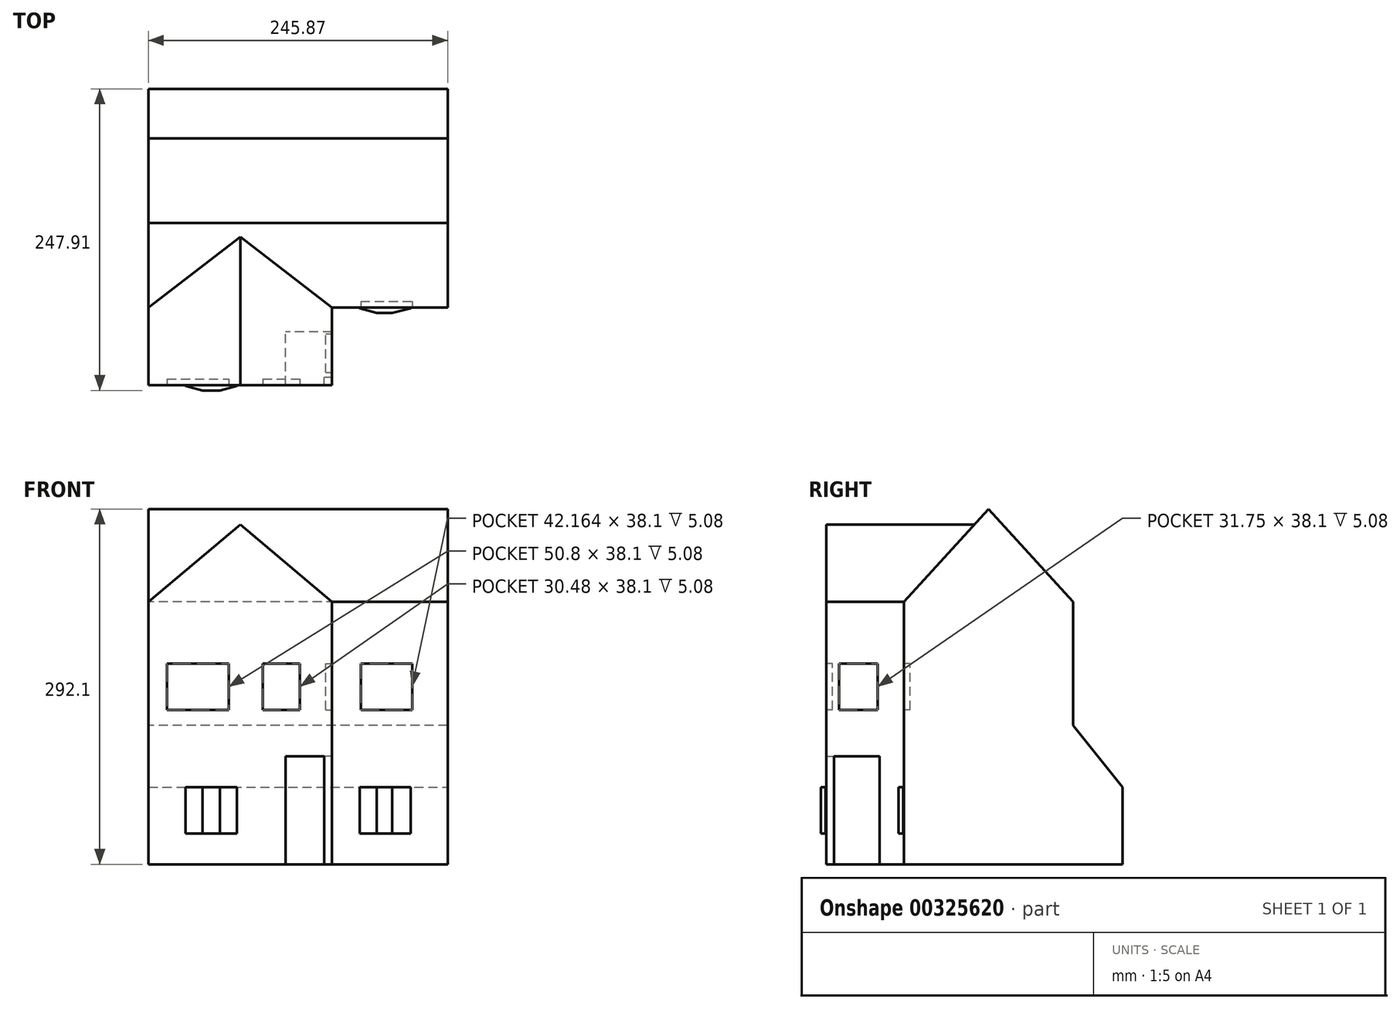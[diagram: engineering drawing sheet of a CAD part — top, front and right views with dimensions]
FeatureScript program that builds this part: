
annotation { "Feature Type Name" : "Feature", "Feature Type Description" : "" }
export const myFeature = defineFeature(function(context is Context, id is Id, definition is map)
    precondition{}
    {
        {
            var Q0;
            Q0=qCreatedBy(makeId("Top.planeOp"),FACE);
            var sketch = newSketch(context, id + "F0", { "sketchPlane" : qUnion([Q0])});
            skLineSegment(sketch, "E0", {"start": v(245.87, 63.75) * mm, "end": v(150.88, 63.75) * mm});
            skLineSegment(sketch, "E1", {"start": v(150.88, 63.75) * mm, "end": v(150.88, 0) * mm});
            skLineSegment(sketch, "E2", {"start": v(150.88, 0) * mm, "end": v(0, 0) * mm});
            skLineSegment(sketch, "E3", {"start": v(0, 0) * mm, "end": v(0, 243.59) * mm});
            skLineSegment(sketch, "E4", {"start": v(0, 243.59) * mm, "end": v(245.87, 243.59) * mm});
            skLineSegment(sketch, "E5", {"start": v(245.87, 243.59) * mm, "end": v(245.87, 63.75) * mm});
            skLineSegment(sketch, "E6.0", {"start": v(6.35, 237.24) * mm, "end": v(239.52, 237.24) * mm});
            skLineSegment(sketch, "E6.1", {"start": v(239.52, 70.1) * mm, "end": v(144.53, 70.1) * mm});
            skLineSegment(sketch, "E6.2", {"start": v(144.53, 70.1) * mm, "end": v(144.53, 6.35) * mm});
            skLineSegment(sketch, "E6.3", {"start": v(239.52, 237.24) * mm, "end": v(239.52, 70.1) * mm});
            skLineSegment(sketch, "E6.4", {"start": v(144.53, 6.35) * mm, "end": v(6.35, 6.35) * mm});
            skLineSegment(sketch, "E6.5", {"start": v(6.35, 6.35) * mm, "end": v(6.35, 237.24) * mm});
            skLineSegment(sketch, "E7", {"start": v(239.52, 195.58) * mm, "end": v(6.35, 195.58) * mm});
            skLineSegment(sketch, "E8.0", {"start": v(239.52, 201.93) * mm, "end": v(6.35, 201.93) * mm});
            skLineSegment(sketch, "E9", {"start": v(144.53, 70.1) * mm, "end": v(144.53, 237.24) * mm});
            skLineSegment(sketch, "E10.0", {"start": v(148.34, 70.1) * mm, "end": v(148.34, 237.24) * mm});
            skLineSegment(sketch, "E11", {"start": v(96.01, 6.35) * mm, "end": v(96.01, 195.58) * mm});
            skLineSegment(sketch, "E12.0", {"start": v(92.2, 6.35) * mm, "end": v(92.2, 195.58) * mm});
            skLineSegment(sketch, "E13", {"start": v(92.2, 153.16) * mm, "end": v(6.35, 153.16) * mm});
            skLineSegment(sketch, "E14.0", {"start": v(92.2, 149.35) * mm, "end": v(6.35, 149.35) * mm});
            skLineSegment(sketch, "E15", {"start": v(88.4, 201.93) * mm, "end": v(88.4, 237.24) * mm});
            skLineSegment(sketch, "E16.0", {"start": v(92.2, 201.93) * mm, "end": v(92.2, 237.24) * mm});
            skSolve(sketch);
        }
        {
            var Q0;
            Q0=makeQuery(id+"F0.imprint","IMPRINT",FACE,{"disambiguationData":[TD([[makeQuery(id+"F0.imprint","IMPRINT",EDGE,{"derivedFrom":sQuery(id+"F0.wireOp",EDGE,"E0")}),-1.0]])]});
            var Q1;
            {var subQ0=sQuery(id+"F0.wireOp",EDGE,"E10.0");var subQ1=sQuery(id+"F0.wireOp",EDGE,"E7");var subQ2=makeQuery(id+"F0.imprint","INTERSECT",VERTEX,{"derivedFrom":[subQ1,subQ0]});Q1=makeQuery(id+"F0.imprint","IMPRINT",FACE,{"disambiguationData":[TD([[makeQuery(id+"F0.imprint","IMPRINT",EDGE,{"disambiguationData":[TD([[subQ2,-1.0]])],"derivedFrom":subQ1}),-1.0]])]});}
            var Q2;
            {var subQ0=sQuery(id+"F0.wireOp",EDGE,"E6.3");var subQ1=sQuery(id+"F0.wireOp",EDGE,"E6.1");var subQ2=makeQuery(id+"F0.imprint","INTERSECT",VERTEX,{"derivedFrom":[subQ1,subQ0]});Q2=makeQuery(id+"F0.imprint","IMPRINT",FACE,{"disambiguationData":[TD([[makeQuery(id+"F0.imprint","IMPRINT",EDGE,{"disambiguationData":[TD([[subQ2,-1.0]])],"derivedFrom":subQ1}),-1.0]])]});}
            var Q3;
            {var subQ0=sQuery(id+"F0.wireOp",EDGE,"E6.3");var subQ1=sQuery(id+"F0.wireOp",EDGE,"E6.0");var subQ2=makeQuery(id+"F0.imprint","INTERSECT",VERTEX,{"derivedFrom":[subQ1,subQ0]});Q3=makeQuery(id+"F0.imprint","IMPRINT",FACE,{"disambiguationData":[TD([[makeQuery(id+"F0.imprint","IMPRINT",EDGE,{"disambiguationData":[TD([[subQ2,1.0]])],"derivedFrom":subQ1}),-1.0]])]});}
            var Q4;
            {var subQ3=sQuery(id+"F0.wireOp",EDGE,"E16.0");Q4=makeQuery(id+"F0.imprint","IMPRINT",FACE,{"disambiguationData":[TD([[makeQuery(id+"F0.imprint","IMPRINT",EDGE,{"derivedFrom":subQ3}),-1.0]])]});}
            var Q5;
            {var subQ3=sQuery(id+"F0.wireOp",EDGE,"E15");Q5=makeQuery(id+"F0.imprint","IMPRINT",FACE,{"disambiguationData":[TD([[makeQuery(id+"F0.imprint","IMPRINT",EDGE,{"derivedFrom":subQ3}),1.0]])]});}
            var Q6;
            {var subQ3=sQuery(id+"F0.wireOp",EDGE,"E13");Q6=makeQuery(id+"F0.imprint","IMPRINT",FACE,{"disambiguationData":[TD([[makeQuery(id+"F0.imprint","IMPRINT",EDGE,{"derivedFrom":subQ3}),-1.0]])]});}
            var Q7;
            {var subQ1=sQuery(id+"F0.wireOp",EDGE,"E6.2");Q7=makeQuery(id+"F0.imprint","IMPRINT",FACE,{"disambiguationData":[TD([[makeQuery(id+"F0.imprint","IMPRINT",EDGE,{"derivedFrom":subQ1}),-1.0]])]});}
            var Q8;
            {var subQ3=sQuery(id+"F0.wireOp",EDGE,"E10.0");var subQ5=sQuery(id+"F0.wireOp",EDGE,"E7");var subQ6=makeQuery(id+"F0.imprint","INTERSECT",VERTEX,{"derivedFrom":[subQ5,subQ3]});Q8=makeQuery(id+"F0.imprint","IMPRINT",FACE,{"disambiguationData":[TD([[makeQuery(id+"F0.imprint","IMPRINT",EDGE,{"disambiguationData":[TD([[subQ6,-1.0]])],"derivedFrom":subQ5}),1.0]])]});}
            var Q9;
            {var subQ5=sQuery(id+"F0.wireOp",EDGE,"E14.0");Q9=makeQuery(id+"F0.imprint","IMPRINT",FACE,{"disambiguationData":[TD([[makeQuery(id+"F0.imprint","IMPRINT",EDGE,{"derivedFrom":subQ5}),1.0]])]});}
            var Q10;
            {var subQ4=sQuery(id+"F0.wireOp",EDGE,"E11");Q10=makeQuery(id+"F0.imprint","IMPRINT",FACE,{"disambiguationData":[TD([[makeQuery(id+"F0.imprint","IMPRINT",EDGE,{"derivedFrom":subQ4}),1.0]])]});}
            var Q11;
            {var subQ0=sQuery(id+"F0.wireOp",EDGE,"E13");Q11=makeQuery(id+"F0.imprint","IMPRINT",FACE,{"disambiguationData":[TD([[makeQuery(id+"F0.imprint","IMPRINT",EDGE,{"derivedFrom":subQ0}),1.0]])]});}
            var Q12;
            {var subQ0=sQuery(id+"F0.wireOp",EDGE,"E7");var subQ1=sQuery(id+"F0.wireOp",EDGE,"E6.3");var subQ2=makeQuery(id+"F0.imprint","INTERSECT",VERTEX,{"derivedFrom":[subQ1,subQ0]});Q12=makeQuery(id+"F0.imprint","IMPRINT",FACE,{"disambiguationData":[TD([[makeQuery(id+"F0.imprint","IMPRINT",EDGE,{"disambiguationData":[TD([[subQ2,1.0]])],"derivedFrom":subQ1}),-1.0]])]});}
            var Q13;
            {var subQ0=sQuery(id+"F0.wireOp",EDGE,"E7");var subQ1=sQuery(id+"F0.wireOp",EDGE,"E6.5");var subQ2=makeQuery(id+"F0.imprint","INTERSECT",VERTEX,{"derivedFrom":[subQ1,subQ0]});Q13=makeQuery(id+"F0.imprint","IMPRINT",FACE,{"disambiguationData":[TD([[makeQuery(id+"F0.imprint","IMPRINT",EDGE,{"disambiguationData":[TD([[subQ2,-1.0]])],"derivedFrom":subQ1}),-1.0]])]});}
            var Q14;
            {var subQ0=sQuery(id+"F0.wireOp",EDGE,"E9");var subQ1=sQuery(id+"F0.wireOp",EDGE,"E6.0");var subQ2=makeQuery(id+"F0.imprint","INTERSECT",VERTEX,{"derivedFrom":[subQ1,subQ0]});Q14=makeQuery(id+"F0.imprint","IMPRINT",FACE,{"disambiguationData":[TD([[makeQuery(id+"F0.imprint","IMPRINT",EDGE,{"disambiguationData":[TD([[subQ2,-1.0]])],"derivedFrom":subQ1}),-1.0]])]});}
            var Q15;
            {var subQ0=sQuery(id+"F0.wireOp",EDGE,"E15");Q15=makeQuery(id+"F0.imprint","IMPRINT",FACE,{"disambiguationData":[TD([[makeQuery(id+"F0.imprint","IMPRINT",EDGE,{"derivedFrom":subQ0}),-1.0]])]});}
            extrude(context, id + "F1", {"entities" : qUnion([Q0, Q1, Q2, Q3, Q4, Q5, Q6, Q7, Q8, Q9, Q10, Q11, Q12, Q13, Q14, Q15]), "depth" : 114.3 * mm});
        }
        {
            var Q0;
            Q0=makeQuery(id+"F1.opExtrude","CAP_EDGE",EDGE,{"disambiguationData":[OSD([sQuery(id+"F0.wireOp",EDGE,"E4")])],"isStart":false});
            chamfer(context, id + "F2", {"entities" : qUnion([Q0]), "chamferType" : ChamferType.TWO_OFFSETS, "width1" : 50.8 * mm, "oppositeDirection" : false, "width2" : 40.64 * mm, "tangentPropagation" : true});
        }
        {
            var Q0;
            Q0=makeQuery(id+"F1.opExtrude","CAP_FACE",FACE,{"disambiguationData":[OSD([sQuery(id+"F0.wireOp",EDGE,"E0"),sQuery(id+"F0.wireOp",EDGE,"E1"),sQuery(id+"F0.wireOp",EDGE,"E2"),sQuery(id+"F0.wireOp",EDGE,"E3"),sQuery(id+"F0.wireOp",EDGE,"E4"),sQuery(id+"F0.wireOp",EDGE,"E5"),sQuery(id+"F0.wireOp",EDGE,"E6.0"),sQuery(id+"F0.wireOp",EDGE,"E6.1"),sQuery(id+"F0.wireOp",EDGE,"E6.2"),sQuery(id+"F0.wireOp",EDGE,"E6.3"),sQuery(id+"F0.wireOp",EDGE,"E6.4"),sQuery(id+"F0.wireOp",EDGE,"E6.5"),sQuery(id+"F0.wireOp",EDGE,"E7"),sQuery(id+"F0.wireOp",EDGE,"E8.0"),sQuery(id+"F0.wireOp",EDGE,"E9"),sQuery(id+"F0.wireOp",EDGE,"E10.0"),sQuery(id+"F0.wireOp",EDGE,"E11"),sQuery(id+"F0.wireOp",EDGE,"E12.0"),sQuery(id+"F0.wireOp",EDGE,"E13"),sQuery(id+"F0.wireOp",EDGE,"E14.0"),sQuery(id+"F0.wireOp",EDGE,"E15"),sQuery(id+"F0.wireOp",EDGE,"E16.0")])],"isStart":false});
            var sketch = newSketch(context, id + "F3", { "sketchPlane" : qUnion([Q0])});
            skLineSegment(sketch, "E17", {"start": v(150.88, 0) * mm, "end": v(0, 0) * mm});
            skLineSegment(sketch, "E18", {"start": v(150.88, 63.75) * mm, "end": v(150.88, 0) * mm});
            skLineSegment(sketch, "E19", {"start": v(245.87, 63.75) * mm, "end": v(150.88, 63.75) * mm});
            skLineSegment(sketch, "E20", {"start": v(245.87, 63.75) * mm, "end": v(245.87, 202.95) * mm});
            skLineSegment(sketch, "E21", {"start": v(0, 202.95) * mm, "end": v(245.87, 202.95) * mm});
            skLineSegment(sketch, "E22", {"start": v(0, 202.95) * mm, "end": v(0, 0) * mm});
            skSolve(sketch);
        }
        {
            var Q0;
            Q0 = qSketchRegion(id + "F3", true);
            extrude(context, id + "F4", {"entities" : qUnion([Q0]), "operationType" : NewBodyOperationType.ADD, "depth" : 101.6 * mm});
        }
        {
            var Q0;
            Q0=makeQuery(id+"F4.boolean.opBoolean","MERGE",FACE,{"derivedFrom":[makeQuery(id+"F1.opExtrude","SWEPT_FACE",FACE,{"disambiguationData":[OSD([sQuery(id+"F0.wireOp",EDGE,"E5")])]}),makeQuery(id+"F4.opExtrude","SWEPT_FACE",FACE,{"disambiguationData":[OSD([sQuery(id+"F3.wireOp",EDGE,"E20")])]})]});
            var sketch = newSketch(context, id + "F5", { "sketchPlane" : qUnion([Q0])});
            skLineSegment(sketch, "E23", {"start": v(63.75, 215.9) * mm, "end": v(133.35, 292.1) * mm});
            skLineSegment(sketch, "E24", {"start": v(133.35, 292.1) * mm, "end": v(202.95, 215.9) * mm});
            skLineSegment(sketch, "E25", {"start": v(202.95, 215.9) * mm, "end": v(63.75, 215.9) * mm});
            skSolve(sketch);
        }
        {
            var Q0;
            Q0 = qSketchRegion(id + "F5", true);
            var Q1;
            Q1=makeQuery(id+"F4.boolean.opBoolean","MERGE",FACE,{"derivedFrom":[makeQuery(id+"F1.opExtrude","SWEPT_FACE",FACE,{"disambiguationData":[OSD([sQuery(id+"F0.wireOp",EDGE,"E3")])]}),makeQuery(id+"F4.opExtrude","SWEPT_FACE",FACE,{"disambiguationData":[OSD([sQuery(id+"F3.wireOp",EDGE,"E22")])]})]});
            extrude(context, id + "F6", {"entities" : qUnion([Q0]), "operationType" : NewBodyOperationType.ADD, "endBound" : BoundingType.UP_TO_SURFACE, "oppositeDirection" : true, "endBoundEntityFace" : qUnion([Q1]), "depth" : 25.4 * mm});
        }
        {
            var Q0;
            Q0=makeQuery(id+"F4.boolean.opBoolean","MERGE",FACE,{"derivedFrom":[makeQuery(id+"F1.opExtrude","SWEPT_FACE",FACE,{"disambiguationData":[OSD([sQuery(id+"F0.wireOp",EDGE,"E2")])]}),makeQuery(id+"F4.opExtrude","SWEPT_FACE",FACE,{"disambiguationData":[OSD([sQuery(id+"F3.wireOp",EDGE,"E17")])]})]});
            var sketch = newSketch(context, id + "F7", { "sketchPlane" : qUnion([Q0])});
            skLineSegment(sketch, "E26", {"start": v(0, 215.9) * mm, "end": v(75.44, 279.4) * mm});
            skLineSegment(sketch, "E27", {"start": v(75.44, 279.4) * mm, "end": v(150.88, 215.9) * mm});
            skLineSegment(sketch, "E28", {"start": v(150.88, 215.9) * mm, "end": v(0, 215.9) * mm});
            skSolve(sketch);
        }
        {
            var Q0;
            Q0 = qSketchRegion(id + "F7", true);
            var Q1;
            Q1=makeQuery(id+"F6.opExtrude","CAP_VERTEX",VERTEX,{"disambiguationData":[OSD([sQuery(id+"F0.wireOp",EDGE,"E3"),sQuery(id+"F3.wireOp",EDGE,"E22"),sQuery(id+"F5.wireOp",EDGE,"E23"),sQuery(id+"F5.wireOp",EDGE,"E24")])],"isStart":false});
            extrude(context, id + "F8", {"entities" : qUnion([Q0]), "operationType" : NewBodyOperationType.ADD, "endBound" : BoundingType.UP_TO_VERTEX, "oppositeDirection" : true, "endBoundEntityVertex" : qUnion([Q1]), "depth" : 25.4 * mm});
        }
        {
            var Q0;
            Q0=makeQuery(id+"F1.opExtrude","CAP_FACE",FACE,{"disambiguationData":[OSD([sQuery(id+"F0.wireOp",EDGE,"E0"),sQuery(id+"F0.wireOp",EDGE,"E1"),sQuery(id+"F0.wireOp",EDGE,"E2"),sQuery(id+"F0.wireOp",EDGE,"E3"),sQuery(id+"F0.wireOp",EDGE,"E4"),sQuery(id+"F0.wireOp",EDGE,"E5")])],"isStart":true});
            var sketch = newSketch(context, id + "F9", { "sketchPlane" : qUnion([Q0])});
            skLineSegment(sketch, "E29.bottom", {"start": v(150.88, 0) * mm, "end": v(112.78, 0) * mm});
            skLineSegment(sketch, "E29.top", {"start": v(150.88, -43.87) * mm, "end": v(112.78, -43.87) * mm});
            skLineSegment(sketch, "E29.left", {"start": v(150.88, 0) * mm, "end": v(150.88, -43.87) * mm});
            skLineSegment(sketch, "E29.right", {"start": v(112.78, 0) * mm, "end": v(112.78, -43.87) * mm});
            skSolve(sketch);
        }
        {
            var Q0;
            Q0 = qSketchRegion(id + "F9", true);
            extrude(context, id + "F10", {"entities" : qUnion([Q0]), "operationType" : NewBodyOperationType.REMOVE, "oppositeDirection" : true, "depth" : 88.9 * mm});
        }
        {
            var Q0;
            Q0=makeQuery(id+"F10.boolean.opBoolean","COPY",FACE,{"derivedFrom":makeQuery(id+"F10.opExtrude","CAP_FACE",FACE,{"disambiguationData":[OSD([sQuery(id+"F9.wireOp",EDGE,"E29.bottom"),sQuery(id+"F9.wireOp",EDGE,"E29.top"),sQuery(id+"F9.wireOp",EDGE,"E29.left"),sQuery(id+"F9.wireOp",EDGE,"E29.right")])],"isStart":false})});
            var sketch = newSketch(context, id + "F11", { "sketchPlane" : qUnion([Q0])});
            skLineSegment(sketch, "E30.bottom", {"start": v(150.88, 0) * mm, "end": v(144.53, 0) * mm});
            skLineSegment(sketch, "E30.top", {"start": v(150.88, -6.35) * mm, "end": v(144.53, -6.35) * mm});
            skLineSegment(sketch, "E30.left", {"start": v(150.88, 0) * mm, "end": v(150.88, -6.35) * mm});
            skLineSegment(sketch, "E30.right", {"start": v(144.53, 0) * mm, "end": v(144.53, -6.35) * mm});
            skSolve(sketch);
        }
        {
            var Q0;
            Q0 = qSketchRegion(id + "F11", true);
            var Q1;
            Q1=makeQuery(id+"F1.opExtrude","CAP_FACE",FACE,{"disambiguationData":[OSD([sQuery(id+"F0.wireOp",EDGE,"E0"),sQuery(id+"F0.wireOp",EDGE,"E1"),sQuery(id+"F0.wireOp",EDGE,"E2"),sQuery(id+"F0.wireOp",EDGE,"E3"),sQuery(id+"F0.wireOp",EDGE,"E4"),sQuery(id+"F0.wireOp",EDGE,"E5")])],"isStart":true});
            extrude(context, id + "F12", {"entities" : qUnion([Q0]), "operationType" : NewBodyOperationType.ADD, "endBound" : BoundingType.UP_TO_SURFACE, "endBoundEntityFace" : qUnion([Q1]), "depth" : 25.4 * mm});
        }
        {
            var Q0;
            Q0=makeQuery(id+"F4.boolean.opBoolean","MERGE",FACE,{"derivedFrom":[makeQuery(id+"F1.opExtrude","SWEPT_FACE",FACE,{"disambiguationData":[OSD([sQuery(id+"F0.wireOp",EDGE,"E0")])]}),makeQuery(id+"F4.opExtrude","SWEPT_FACE",FACE,{"disambiguationData":[OSD([sQuery(id+"F3.wireOp",EDGE,"E19")])]})]});
            var sketch = newSketch(context, id + "F13", { "sketchPlane" : qUnion([Q0])});
            skLineSegment(sketch, "E31.bottom", {"start": v(173.48, 25.4) * mm, "end": v(215.65, 25.4) * mm});
            skLineSegment(sketch, "E31.top", {"start": v(173.48, 63.5) * mm, "end": v(215.65, 63.5) * mm});
            skLineSegment(sketch, "E31.left", {"start": v(173.48, 25.4) * mm, "end": v(173.48, 63.5) * mm});
            skLineSegment(sketch, "E31.right", {"start": v(215.65, 25.4) * mm, "end": v(215.65, 63.5) * mm});
            skLineSegment(sketch, "E32.bottom", {"start": v(174.5, 127) * mm, "end": v(216.66, 127) * mm});
            skLineSegment(sketch, "E32.top", {"start": v(174.5, 165.1) * mm, "end": v(216.66, 165.1) * mm});
            skLineSegment(sketch, "E32.left", {"start": v(174.5, 127) * mm, "end": v(174.5, 165.1) * mm});
            skLineSegment(sketch, "E32.right", {"start": v(216.66, 127) * mm, "end": v(216.66, 165.1) * mm});
            skSolve(sketch);
        }
        {
            var Q0;
            Q0=makeQuery(id+"F13.imprint","IMPRINT",FACE,{"disambiguationData":[TD([[makeQuery(id+"F13.imprint","IMPRINT",EDGE,{"derivedFrom":sQuery(id+"F13.wireOp",EDGE,"E31.bottom")}),1.0]])]});
            extrude(context, id + "F14", {"entities" : qUnion([Q0]), "operationType" : NewBodyOperationType.ADD, "depth" : 4.32 * mm});
        }
        {
            var Q0;
            Q0=makeQuery(id+"F14.opExtrude","CAP_EDGE",EDGE,{"disambiguationData":[OSD([sQuery(id+"F13.wireOp",EDGE,"E31.right")])],"isStart":false});
            chamfer(context, id + "F15", {"entities" : qUnion([Q0]), "chamferType" : ChamferType.TWO_OFFSETS, "width1" : 15.24 * mm, "oppositeDirection" : false, "width2" : 3.8 * mm, "tangentPropagation" : true});
        }
        {
            var Q0;
            Q0=makeQuery(id+"F14.opExtrude","CAP_EDGE",EDGE,{"disambiguationData":[OSD([sQuery(id+"F13.wireOp",EDGE,"E31.left")])],"isStart":false});
            chamfer(context, id + "F16", {"entities" : qUnion([Q0]), "chamferType" : ChamferType.TWO_OFFSETS, "width1" : 3.8 * mm, "oppositeDirection" : false, "width2" : 13.97 * mm, "tangentPropagation" : true});
        }
        {
            var Q0;
            Q0=makeQuery(id+"F13.imprint","IMPRINT",FACE,{"disambiguationData":[TD([[makeQuery(id+"F13.imprint","IMPRINT",EDGE,{"derivedFrom":sQuery(id+"F13.wireOp",EDGE,"E32.bottom")}),1.0]])]});
            extrude(context, id + "F17", {"entities" : qUnion([Q0]), "operationType" : NewBodyOperationType.REMOVE, "oppositeDirection" : true, "depth" : 5.08 * mm});
        }
        {
            var Q0;
            Q0=makeQuery(id+"F12.boolean.opBoolean","MERGE",FACE,{"derivedFrom":[makeQuery(id+"F8.boolean.opBoolean","MERGE",FACE,{"derivedFrom":[makeQuery(id+"F4.boolean.opBoolean","MERGE",FACE,{"derivedFrom":[makeQuery(id+"F1.opExtrude","SWEPT_FACE",FACE,{"disambiguationData":[OSD([sQuery(id+"F0.wireOp",EDGE,"E2")])]}),makeQuery(id+"F4.opExtrude","SWEPT_FACE",FACE,{"disambiguationData":[OSD([sQuery(id+"F3.wireOp",EDGE,"E17")])]})]}),makeQuery(id+"F8.opExtrude","CAP_FACE",FACE,{"disambiguationData":[OSD([sQuery(id+"F7.wireOp",EDGE,"E26"),sQuery(id+"F7.wireOp",EDGE,"E27"),sQuery(id+"F7.wireOp",EDGE,"E28")])],"isStart":true})]}),makeQuery(id+"F12.opExtrude","SWEPT_FACE",FACE,{"disambiguationData":[OSD([sQuery(id+"F11.wireOp",EDGE,"E30.bottom")])]})]});
            var sketch = newSketch(context, id + "F18", { "sketchPlane" : qUnion([Q0])});
            skLineSegment(sketch, "E33.bottom", {"start": v(30.48, 25.4) * mm, "end": v(72.64, 25.4) * mm});
            skLineSegment(sketch, "E33.top", {"start": v(30.48, 63.5) * mm, "end": v(72.64, 63.5) * mm});
            skLineSegment(sketch, "E33.left", {"start": v(30.48, 25.4) * mm, "end": v(30.48, 63.5) * mm});
            skLineSegment(sketch, "E33.right", {"start": v(72.64, 25.4) * mm, "end": v(72.64, 63.5) * mm});
            skLineSegment(sketch, "E34.bottom", {"start": v(15.24, 127) * mm, "end": v(66.04, 127) * mm});
            skLineSegment(sketch, "E34.top", {"start": v(15.24, 165.1) * mm, "end": v(66.04, 165.1) * mm});
            skLineSegment(sketch, "E34.left", {"start": v(15.24, 127) * mm, "end": v(15.24, 165.1) * mm});
            skLineSegment(sketch, "E34.right", {"start": v(66.04, 127) * mm, "end": v(66.04, 165.1) * mm});
            skLineSegment(sketch, "E35.bottom", {"start": v(93.98, 127) * mm, "end": v(124.46, 127) * mm});
            skLineSegment(sketch, "E35.top", {"start": v(93.98, 165.1) * mm, "end": v(124.46, 165.1) * mm});
            skLineSegment(sketch, "E35.left", {"start": v(93.98, 127) * mm, "end": v(93.98, 165.1) * mm});
            skLineSegment(sketch, "E35.right", {"start": v(124.46, 127) * mm, "end": v(124.46, 165.1) * mm});
            skLineSegment(sketch, "E36", {"start": v(66.04, 127) * mm, "end": v(93.98, 127) * mm, "construction": true});
            skSolve(sketch);
        }
        {
            var Q0;
            Q0=makeQuery(id+"F18.imprint","IMPRINT",FACE,{"disambiguationData":[TD([[makeQuery(id+"F18.imprint","IMPRINT",EDGE,{"derivedFrom":sQuery(id+"F18.wireOp",EDGE,"E33.bottom")}),1.0]])]});
            extrude(context, id + "F19", {"entities" : qUnion([Q0]), "operationType" : NewBodyOperationType.ADD, "depth" : 4.32 * mm});
        }
        {
            var Q0;
            Q0=makeQuery(id+"F19.opExtrude","CAP_EDGE",EDGE,{"disambiguationData":[OSD([sQuery(id+"F18.wireOp",EDGE,"E33.right")])],"isStart":false});
            chamfer(context, id + "F20", {"entities" : qUnion([Q0]), "chamferType" : ChamferType.TWO_OFFSETS, "width1" : 3.8 * mm, "oppositeDirection" : true, "width2" : 13.97 * mm, "tangentPropagation" : true});
        }
        {
            var Q0;
            Q0=makeQuery(id+"F19.opExtrude","CAP_EDGE",EDGE,{"disambiguationData":[OSD([sQuery(id+"F18.wireOp",EDGE,"E33.left")])],"isStart":false});
            chamfer(context, id + "F21", {"entities" : qUnion([Q0]), "chamferType" : ChamferType.TWO_OFFSETS, "width1" : 3.8 * mm, "oppositeDirection" : false, "width2" : 13.97 * mm, "tangentPropagation" : true});
        }
        {
            var Q0;
            Q0=makeQuery(id+"F18.imprint","IMPRINT",FACE,{"disambiguationData":[TD([[makeQuery(id+"F18.imprint","IMPRINT",EDGE,{"derivedFrom":sQuery(id+"F18.wireOp",EDGE,"E34.bottom")}),1.0]])]});
            extrude(context, id + "F22", {"entities" : qUnion([Q0]), "operationType" : NewBodyOperationType.REMOVE, "oppositeDirection" : true, "depth" : 5.08 * mm});
        }
        {
            var Q0;
            Q0=makeQuery(id+"F18.imprint","IMPRINT",FACE,{"disambiguationData":[TD([[makeQuery(id+"F18.imprint","IMPRINT",EDGE,{"derivedFrom":sQuery(id+"F18.wireOp",EDGE,"E35.bottom")}),1.0]])]});
            extrude(context, id + "F23", {"entities" : qUnion([Q0]), "operationType" : NewBodyOperationType.REMOVE, "oppositeDirection" : true, "depth" : 5.08 * mm});
        }
        {
            var Q0;
            Q0=makeQuery(id+"F12.boolean.opBoolean","MERGE",FACE,{"derivedFrom":[makeQuery(id+"F4.boolean.opBoolean","MERGE",FACE,{"derivedFrom":[makeQuery(id+"F1.opExtrude","SWEPT_FACE",FACE,{"disambiguationData":[OSD([sQuery(id+"F0.wireOp",EDGE,"E1")])]}),makeQuery(id+"F4.opExtrude","SWEPT_FACE",FACE,{"disambiguationData":[OSD([sQuery(id+"F3.wireOp",EDGE,"E18")])]})]}),makeQuery(id+"F12.opExtrude","SWEPT_FACE",FACE,{"disambiguationData":[OSD([sQuery(id+"F11.wireOp",EDGE,"E30.left")])]})]});
            var sketch = newSketch(context, id + "F24", { "sketchPlane" : qUnion([Q0])});
            skLineSegment(sketch, "E37.bottom", {"start": v(10.41, 126.88) * mm, "end": v(42.16, 126.88) * mm});
            skLineSegment(sketch, "E37.top", {"start": v(10.41, 164.98) * mm, "end": v(42.16, 164.98) * mm});
            skLineSegment(sketch, "E37.left", {"start": v(10.41, 126.88) * mm, "end": v(10.41, 164.98) * mm});
            skLineSegment(sketch, "E37.right", {"start": v(42.16, 126.88) * mm, "end": v(42.16, 164.98) * mm});
            skSolve(sketch);
        }
        {
            var Q0;
            Q0=makeQuery(id+"F24.imprint","IMPRINT",FACE,{"disambiguationData":[TD([[makeQuery(id+"F24.imprint","IMPRINT",EDGE,{"derivedFrom":sQuery(id+"F24.wireOp",EDGE,"E37.bottom")}),1.0]])]});
            extrude(context, id + "F25", {"entities" : qUnion([Q0]), "operationType" : NewBodyOperationType.REMOVE, "oppositeDirection" : true, "depth" : 5.08 * mm});
        }
    });
